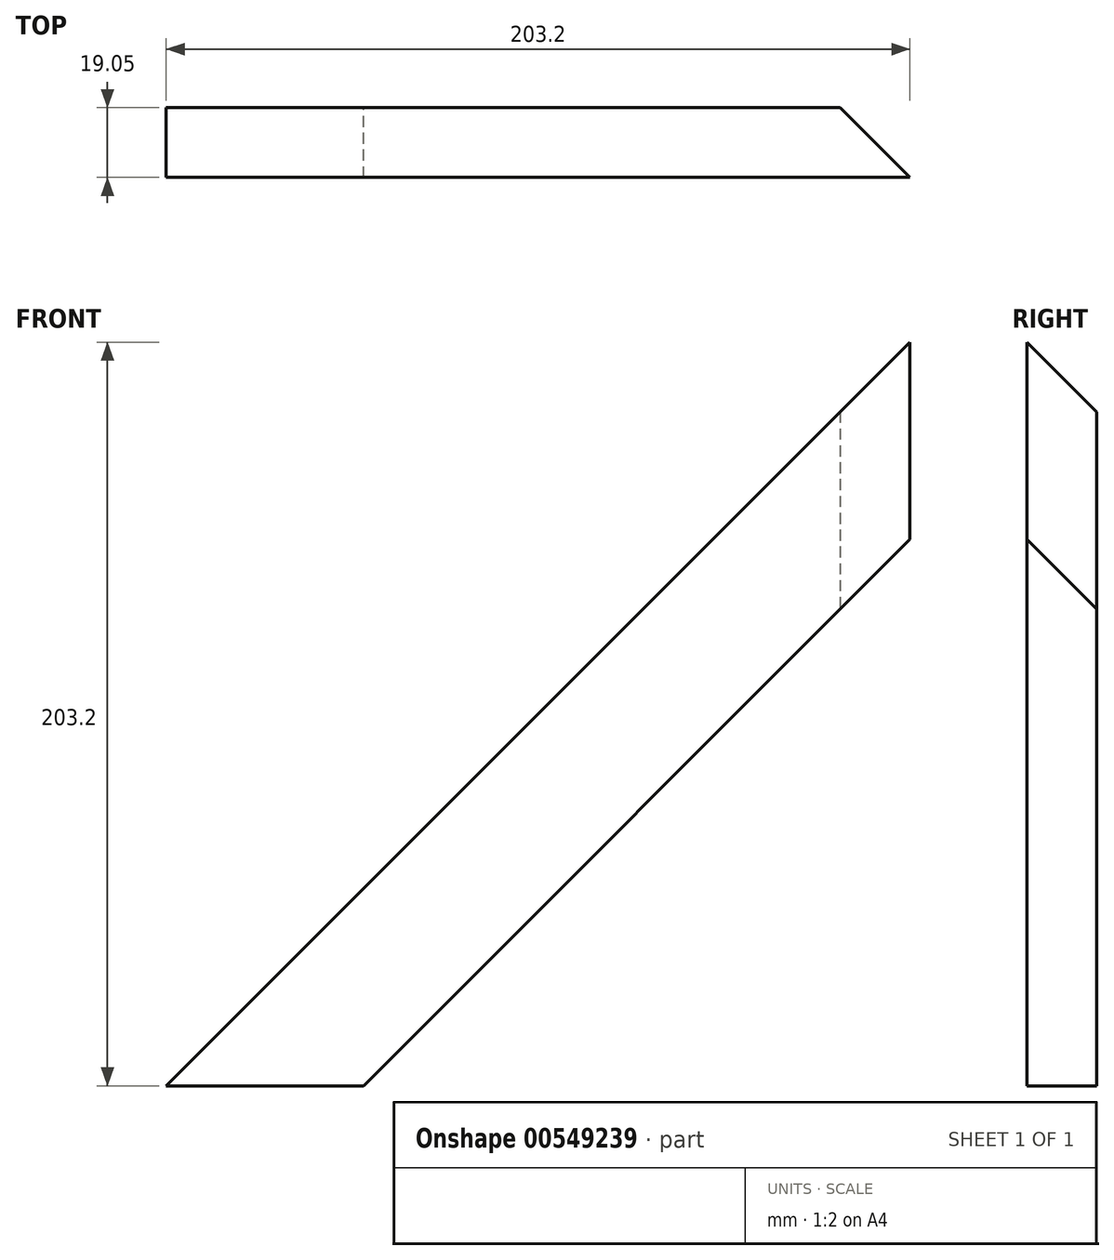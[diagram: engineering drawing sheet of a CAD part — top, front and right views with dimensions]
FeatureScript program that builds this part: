
annotation { "Feature Type Name" : "Feature", "Feature Type Description" : "" }
export const myFeature = defineFeature(function(context is Context, id is Id, definition is map)
    precondition{}
    {
        {
            var Q0;
            Q0=qCreatedBy(makeId("Front.planeOp"),FACE);
            var sketch = newSketch(context, id + "F0", { "sketchPlane" : qUnion([Q0])});
            skLineSegment(sketch, "E0", {"start": v(0, 0) * mm, "end": v(53.88, 0) * mm});
            skLineSegment(sketch, "E1", {"start": v(53.88, 0) * mm, "end": v(203.2, 149.32) * mm});
            skLineSegment(sketch, "E2", {"start": v(203.2, 149.32) * mm, "end": v(203.2, 203.2) * mm});
            skLineSegment(sketch, "E3", {"start": v(203.2, 203.2) * mm, "end": v(0, 0) * mm});
            skSolve(sketch);
        }
        {
            var Q0;
            Q0=qSketchRegion(id+"F0",true);
            extrude(context, id + "F1", {"entities" : qUnion([Q0]), "depth" : 19.05 * mm, "offsetDistance" : 25.4 * mm});
        }
        {
            var Q0;
            Q0=qCreatedBy(makeId("Top.planeOp"),FACE);
            var sketch = newSketch(context, id + "F2", { "sketchPlane" : qUnion([Q0])});
            skLineSegment(sketch, "E4", {"start": v(203.2, -19.05) * mm, "end": v(184.15, 0) * mm});
            skLineSegment(sketch, "E5", {"start": v(184.15, 0) * mm, "end": v(203.2, 0) * mm});
            skLineSegment(sketch, "E6", {"start": v(203.2, 0) * mm, "end": v(203.2, -19.05) * mm});
            skSolve(sketch);
        }
        {
            var Q0;
            Q0 = qSketchRegion(id + "F2", true);
            extrude(context, id + "F3", {"entities" : qUnion([Q0]), "operationType" : NewBodyOperationType.REMOVE, "endBound" : BoundingType.THROUGH_ALL, "depth" : 25.4 * mm, "offsetDistance" : 25.4 * mm});
        }
    });
